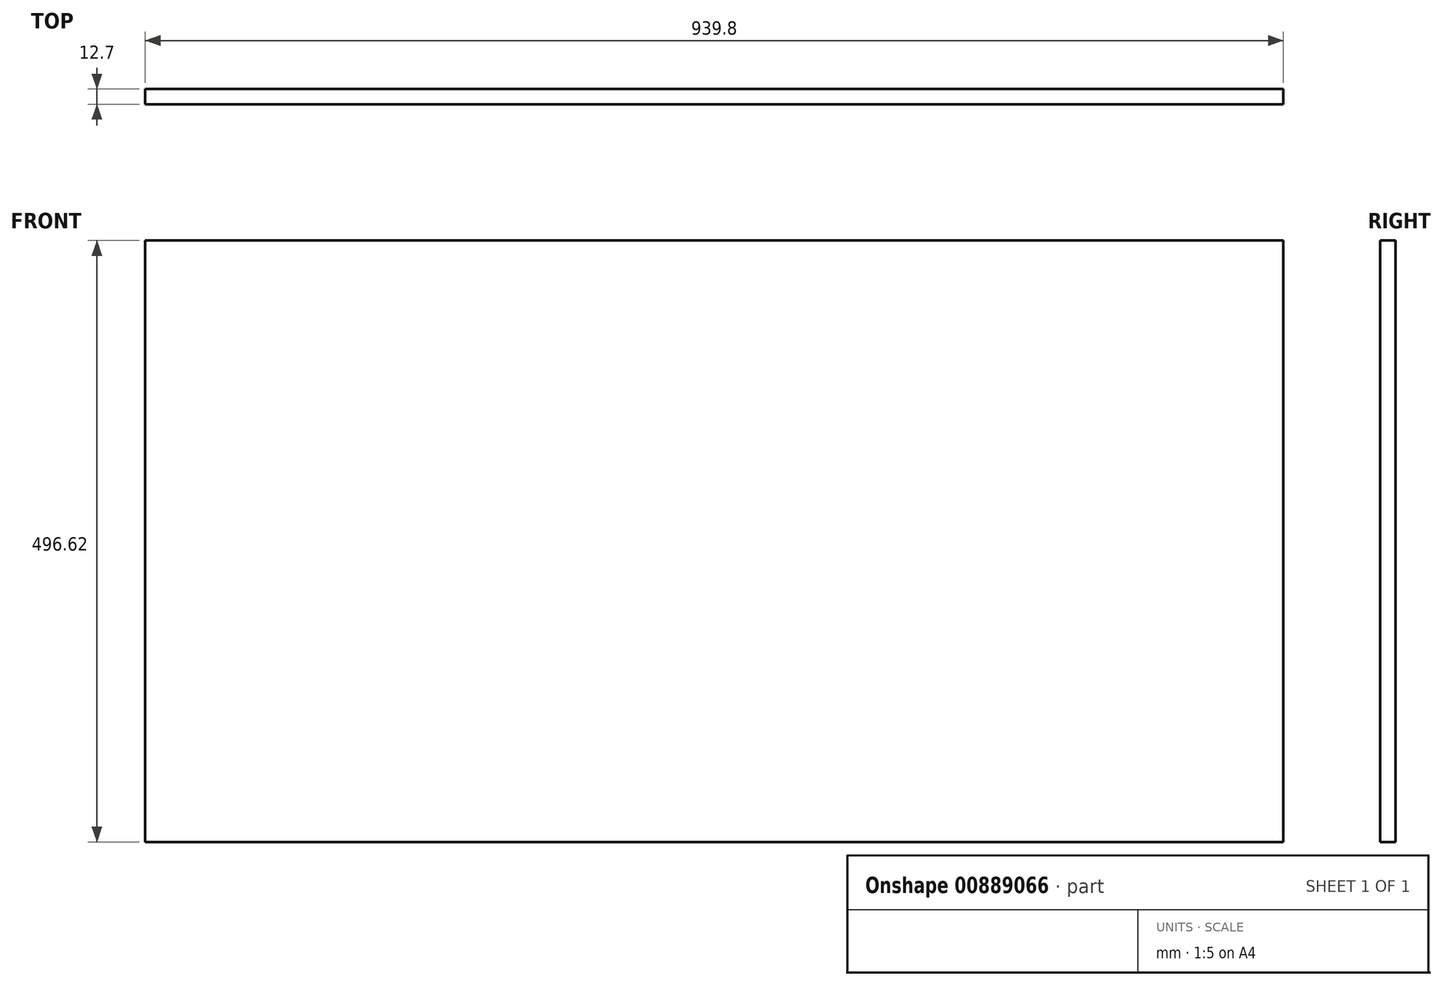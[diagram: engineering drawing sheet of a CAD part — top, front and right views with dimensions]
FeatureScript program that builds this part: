
annotation { "Feature Type Name" : "Feature", "Feature Type Description" : "" }
export const myFeature = defineFeature(function(context is Context, id is Id, definition is map)
    precondition{}
    {
        {
            var Q0;
            Q0=qCreatedBy(makeId("Front.planeOp"),FACE);
            var sketch = newSketch(context, id + "F0", { "sketchPlane" : qUnion([Q0])});
            skLineSegment(sketch, "E0.bottom", {"start": v(-469.9, 248.31) * mm, "end": v(469.9, 248.31) * mm});
            skLineSegment(sketch, "E0.top", {"start": v(-469.9, -248.31) * mm, "end": v(469.9, -248.31) * mm});
            skLineSegment(sketch, "E0.left", {"start": v(-469.9, 248.31) * mm, "end": v(-469.9, -248.31) * mm});
            skLineSegment(sketch, "E0.right", {"start": v(469.9, 248.31) * mm, "end": v(469.9, -248.31) * mm});
            skPoint(sketch, "E0.middle", {"position": v(0, 0) * mm});
            skSolve(sketch);
        }
        {
            var Q0;
            Q0 = qSketchRegion(id + "F0", true);
            extrude(context, id + "F1", {"entities" : qUnion([Q0]), "depth" : 12.7 * mm, "offsetDistance" : 25.4 * mm});
        }
    });
